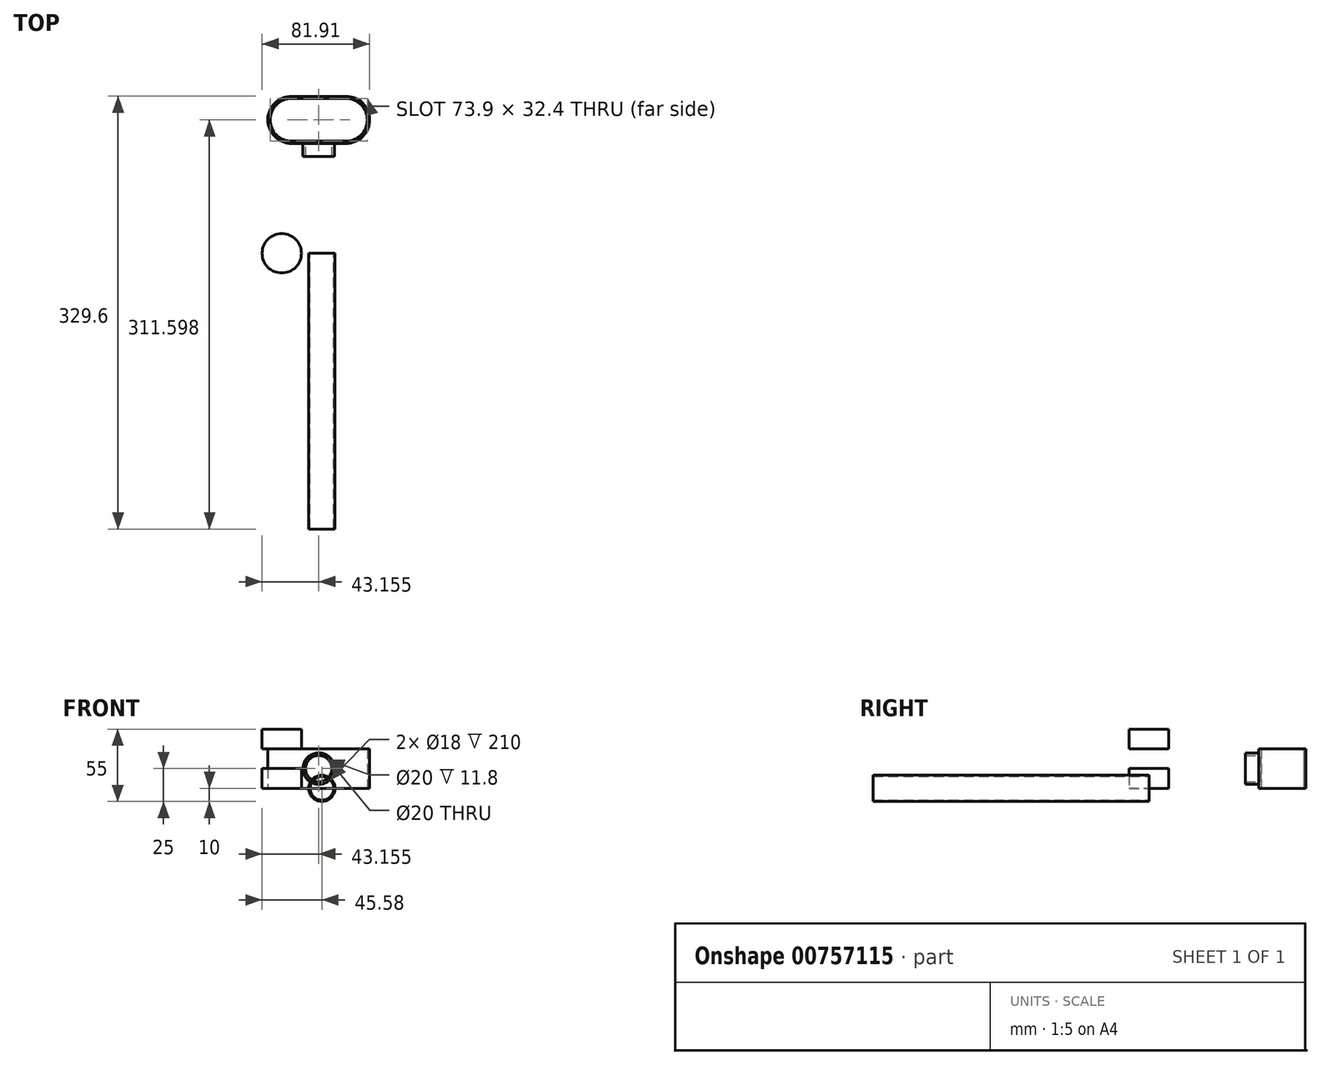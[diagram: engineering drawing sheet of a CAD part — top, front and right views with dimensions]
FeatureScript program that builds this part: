
annotation { "Feature Type Name" : "Feature", "Feature Type Description" : "" }
export const myFeature = defineFeature(function(context is Context, id is Id, definition is map)
    precondition{}
    {
        {
            var Q0;
            Q0=qCreatedBy(makeId("Front.planeOp"),FACE);
            var sketch = newSketch(context, id + "F0", { "sketchPlane" : qUnion([Q0])});
            skCircle(sketch, "E0", {"center": v(0, 0) * mm, "radius": 10 * mm});
            skCircle(sketch, "E1", {"center": v(0, 0) * mm, "radius": 9 * mm});
            skSolve(sketch);
        }
        {
            var Q0;
            Q0 = qSketchRegion(id + "F0", true);
            extrude(context, id + "F1", {"entities" : qUnion([Q0]), "depth" : 210 * mm, "offsetDistance" : 25 * mm});
        }
        {
            var Q0;
            Q0=qCreatedBy(makeId("Top.planeOp"),FACE);
            var sketch = newSketch(context, id + "F2", { "sketchPlane" : qUnion([Q0])});
            skCircle(sketch, "E2", {"center": v(-30.58, 0) * mm, "radius": 15 * mm});
            skSolve(sketch);
        }
        {
            var Q0;
            Q0 = qSketchRegion(id + "F2", true);
            extrude(context, id + "F3", {"entities" : qUnion([Q0]), "depth" : 15 * mm, "offsetDistance" : 25 * mm});
        }
        {
            var Q0;
            Q0=makeQuery(id+"F3.opExtrude","SWEPT_BODY",BODY,{"disambiguationData":[OSD([sQuery(id+"F2.wireOp",EDGE,"E2")])]});
            transform(context, id + "F4", {"entities" : qUnion([Q0]), "transformType" : TransformType.TRANSLATION_3D, "dx" : 0 * mm, "dy" : 0 * mm, "dz" : 30 * mm, "makeCopy" : true});
        }
        {
            var Q0;
            Q0=qCreatedBy(makeId("Top.planeOp"),FACE);
            var sketch = newSketch(context, id + "F5", { "sketchPlane" : qUnion([Q0])});
            skPoint(sketch, "E3.middle", {"position": v(0, 101.6) * mm});
            skArc(sketch, "E4", {"start": v(-23.18, 119.6) * mm, "mid": v(-41.18, 101.6) * mm, "end": v(-23.18, 83.6) * mm});
            skLineSegment(sketch, "E5", {"start": v(-45.35, 101.6) * mm, "end": v(35.65, 101.6) * mm, "construction": true});
            skArc(sketch, "E6.MirrorC", {"start": v(18.32, 119.6) * mm, "mid": v(36.32, 101.6) * mm, "end": v(18.32, 83.6) * mm});
            skLineSegment(sketch, "E7", {"start": v(-23.18, 119.6) * mm, "end": v(18.32, 119.6) * mm});
            skLineSegment(sketch, "E8.MirrorCS", {"start": v(-23.18, 83.6) * mm, "end": v(18.32, 83.6) * mm});
            skArc(sketch, "E9", {"start": v(-23.18, 117.8) * mm, "mid": v(-39.38, 101.6) * mm, "end": v(-23.18, 85.4) * mm});
            skLineSegment(sketch, "E10", {"start": v(-23.18, 119.6) * mm, "end": v(-23.18, 83.6) * mm, "construction": true});
            skLineSegment(sketch, "E11", {"start": v(-2.43, 119.6) * mm, "end": v(-2.43, 83.6) * mm, "construction": true});
            skLineSegment(sketch, "E12", {"start": v(-23.18, 117.8) * mm, "end": v(0, 117.8) * mm});
            skLineSegment(sketch, "E13", {"start": v(-23.18, 85.4) * mm, "end": v(0, 85.4) * mm});
            skLineSegment(sketch, "E14.MirrorCS", {"start": v(18.32, 117.8) * mm, "end": v(-4.85, 117.8) * mm});
            skArc(sketch, "E15.MirrorCS", {"start": v(18.32, 117.8) * mm, "mid": v(34.52, 101.6) * mm, "end": v(18.32, 85.4) * mm});
            skLineSegment(sketch, "E16.MirrorCS", {"start": v(18.32, 85.4) * mm, "end": v(-4.85, 85.4) * mm});
            skSolve(sketch);
        }
        {
            var Q0;
            Q0 = qSketchRegion(id + "F5", true);
            extrude(context, id + "F6", {"entities" : qUnion([Q0]), "depth" : 30 * mm, "offsetDistance" : 25 * mm});
        }
        {
            var Q0;
            Q0=makeQuery(id+"F6.opExtrude","SWEPT_FACE",FACE,{"disambiguationData":[OSD([sQuery(id+"F5.wireOp",EDGE,"E8.MirrorCS")])]});
            var sketch = newSketch(context, id + "F7", { "sketchPlane" : qUnion([Q0])});
            skLineSegment(sketch, "E17", {"start": v(-2.43, 30) * mm, "end": v(-2.43, 0) * mm, "construction": true});
            skLineSegment(sketch, "E18", {"start": v(-23.18, 15) * mm, "end": v(18.32, 15) * mm, "construction": true});
            skCircle(sketch, "E19", {"center": v(-2.43, 15) * mm, "radius": 12 * mm});
            skCircle(sketch, "E20", {"center": v(-2.43, 15) * mm, "radius": 10 * mm});
            skSolve(sketch);
        }
        {
            var Q0;
            Q0 = qSketchRegion(id + "F7", true);
            extrude(context, id + "F8", {"entities" : qUnion([Q0]), "operationType" : NewBodyOperationType.ADD, "depth" : 10 * mm, "offsetDistance" : 25 * mm});
        }
        {
            var Q0;
            Q0=makeQuery(id+"F8.boolean.opBoolean","SPLIT",FACE,{"disambiguationData":[TD([makeQuery(id+"F8.opExtrude","SWEPT_FACE",FACE,{"disambiguationData":[OSD([sQuery(id+"F7.wireOp",EDGE,"E20")])]})])],"derivedFrom":makeQuery(id+"F6.opExtrude","SWEPT_FACE",FACE,{"disambiguationData":[OSD([sQuery(id+"F5.wireOp",EDGE,"E8.MirrorCS")])]})});
            var sketch = newSketch(context, id + "F9", { "sketchPlane" : qUnion([Q0])});
            skCircle(sketch, "E21", {"center": v(-2.43, 15) * mm, "radius": 10 * mm});
            skSolve(sketch);
        }
        {
            var Q0;
            Q0 = qSketchRegion(id + "F9", true);
            extrude(context, id + "F10", {"entities" : qUnion([Q0]), "operationType" : NewBodyOperationType.REMOVE, "endBound" : BoundingType.THROUGH_ALL, "oppositeDirection" : true, "depth" : 25 * mm, "offsetDistance" : 25 * mm});
        }
    });
